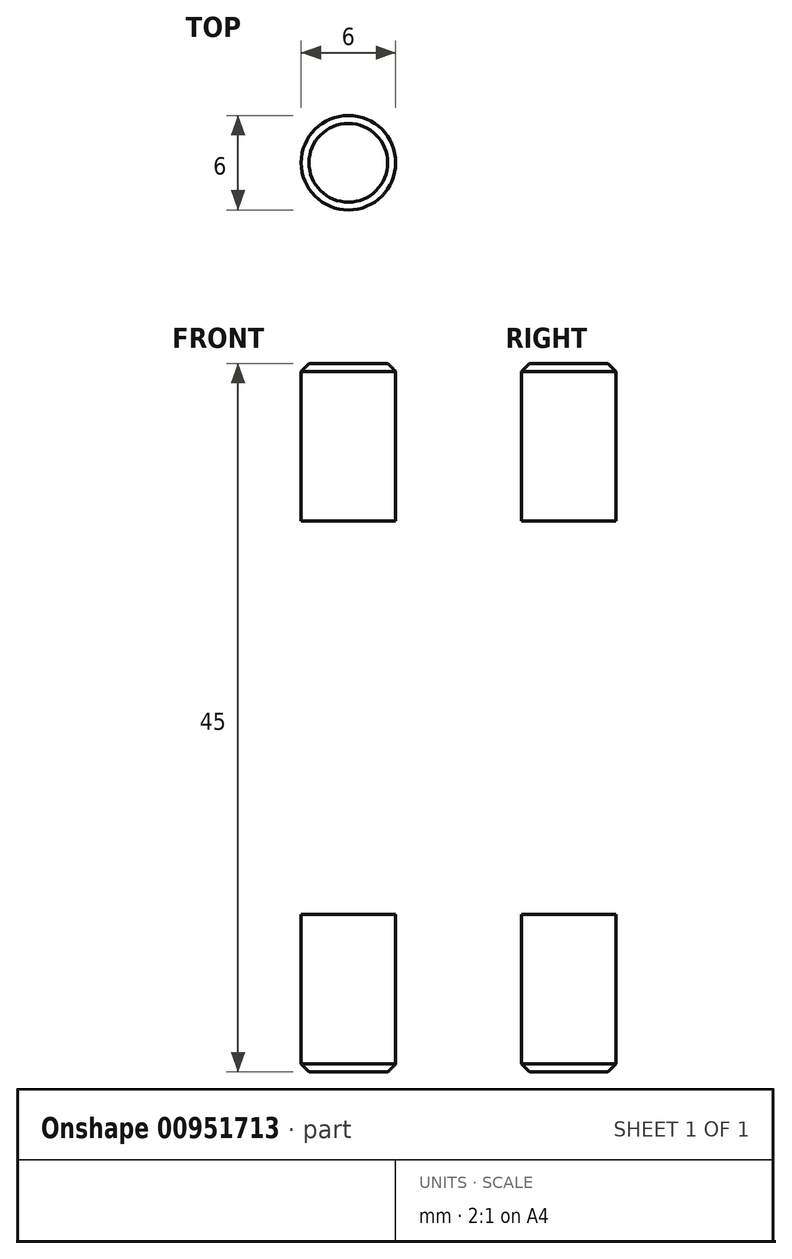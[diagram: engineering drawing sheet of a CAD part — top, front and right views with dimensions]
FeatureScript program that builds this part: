
annotation { "Feature Type Name" : "Feature", "Feature Type Description" : "" }
export const myFeature = defineFeature(function(context is Context, id is Id, definition is map)
    precondition{}
    {
        {
            var Q0;
            Q0=qCreatedBy(makeId("Right.planeOp"),FACE);
            var sketch = newSketch(context, id + "F0", { "sketchPlane" : qUnion([Q0])});
            skLineSegment(sketch, "E0.bottom", {"start": v(-12.5, 12.5) * mm, "end": v(12.5, 12.5) * mm});
            skLineSegment(sketch, "E0.top", {"start": v(-12.5, -12.5) * mm, "end": v(12.5, -12.5) * mm});
            skLineSegment(sketch, "E0.left", {"start": v(-12.5, 12.5) * mm, "end": v(-12.5, -12.5) * mm});
            skLineSegment(sketch, "E0.right", {"start": v(12.5, 12.5) * mm, "end": v(12.5, -12.5) * mm});
            skPoint(sketch, "E0.middle", {"position": v(0, 0) * mm});
            skLineSegment(sketch, "E1.bottom", {"start": v(-3, 22.5) * mm, "end": v(3, 22.5) * mm});
            skLineSegment(sketch, "E1.top", {"start": v(-3, -22.5) * mm, "end": v(3, -22.5) * mm});
            skLineSegment(sketch, "E1.left", {"start": v(-3, 22.5) * mm, "end": v(-3, 12.5) * mm});
            skLineSegment(sketch, "E2.left", {"start": v(-12.5, 5) * mm, "end": v(-12.5, -5) * mm});
            skLineSegment(sketch, "E2.right", {"start": v(12.5, 5) * mm, "end": v(12.5, -5) * mm});
            skLineSegment(sketch, "E3.trimOffspring", {"start": v(-3, -12.5) * mm, "end": v(-3, -22.5) * mm});
            skLineSegment(sketch, "E4.trimOffspring", {"start": v(3, -12.5) * mm, "end": v(3, -22.5) * mm});
            skLineSegment(sketch, "E5", {"start": v(3, 22.5) * mm, "end": v(3, 12.5) * mm});
            skLineSegment(sketch, "E6", {"start": v(0, 22.5) * mm, "end": v(0, -22.5) * mm});
            skSolve(sketch);
        }
        {
            var Q0;
            {var subQ9=sQuery(id+"F0.wireOp",EDGE,"E2.right");Q0=makeQuery(id+"F0.imprint","IMPRINT",FACE,{"disambiguationData":[TD([[makeQuery(id+"F0.imprint","IMPRINT",EDGE,{"derivedFrom":subQ9}),-1.0]])]});}
            var Q1;
            {var subQ0=sQuery(id+"F0.wireOp",EDGE,"E5");Q1=makeQuery(id+"F0.imprint","IMPRINT",FACE,{"disambiguationData":[TD([[makeQuery(id+"F0.imprint","IMPRINT",EDGE,{"derivedFrom":subQ0}),-1.0]])]});}
            var Q2;
            {var subQ0=sQuery(id+"F0.wireOp",EDGE,"E4.trimOffspring");Q2=makeQuery(id+"F0.imprint","IMPRINT",FACE,{"disambiguationData":[TD([[makeQuery(id+"F0.imprint","IMPRINT",EDGE,{"derivedFrom":subQ0}),-1.0]])]});}
            var Q3;
            Q3=sQuery(id+"F0.wireOp",EDGE,"E6");
            revolve(context, id + "F1", {"surfaceOperationType" : NewSurfaceOperationType.NEW, "entities" : qUnion([Q0, Q1, Q2]), "axis" : qUnion([Q3]), "revolveType" : RevolveType.FULL});
        }
        {
            var Q0;
            Q0=qCreatedBy(makeId("Right.planeOp"),FACE);
            var sketch = newSketch(context, id + "F2", { "sketchPlane" : qUnion([Q0])});
            skCircle(sketch, "E7", {"center": v(0, 0) * mm, "radius": 5 * mm});
            skSolve(sketch);
        }
        {
            var Q0;
            Q0 = qSketchRegion(id + "F2", true);
            extrude(context, id + "F3", {"entities" : qUnion([Q0]), "operationType" : NewBodyOperationType.REMOVE, "depth" : 25 * mm, "offsetDistance" : 25 * mm, "symmetric" : true});
        }
        {
            var Q0;
            Q0=qCreatedBy(makeId("Right.planeOp"),FACE);
            var sketch = newSketch(context, id + "F4", { "sketchPlane" : qUnion([Q0])});
            skCircle(sketch, "E8", {"center": v(0, 0) * mm, "radius": 7 * mm});
            skSolve(sketch);
        }
        {
            var Q0;
            Q0 = qSketchRegion(id + "F4", true);
            extrude(context, id + "F5", {"entities" : qUnion([Q0]), "operationType" : NewBodyOperationType.REMOVE, "depth" : 14 * mm, "offsetDistance" : 25 * mm, "hasSecondDirection" : true, "secondDirectionOppositeDirection" : false, "secondDirectionDepth" : 9 * mm});
        }
        {
            var Q0;
            Q0=makeQuery(id+"F1.opRevolve","SWEPT_EDGE",EDGE,{"disambiguationData":[OSD([sQuery(id+"F0.wireOp",EDGE,"E1.bottom"),sQuery(id+"F0.wireOp",EDGE,"E5")])]});
            var Q1;
            Q1=makeQuery(id+"F1.opRevolve","SWEPT_EDGE",EDGE,{"disambiguationData":[OSD([sQuery(id+"F0.wireOp",EDGE,"E1.top"),sQuery(id+"F0.wireOp",EDGE,"E4.trimOffspring")])]});
            chamfer(context, id + "F6", {"entities" : qUnion([Q0, Q1]), "width" : .5 * mm, "tangentPropagation" : true});
        }
    });
